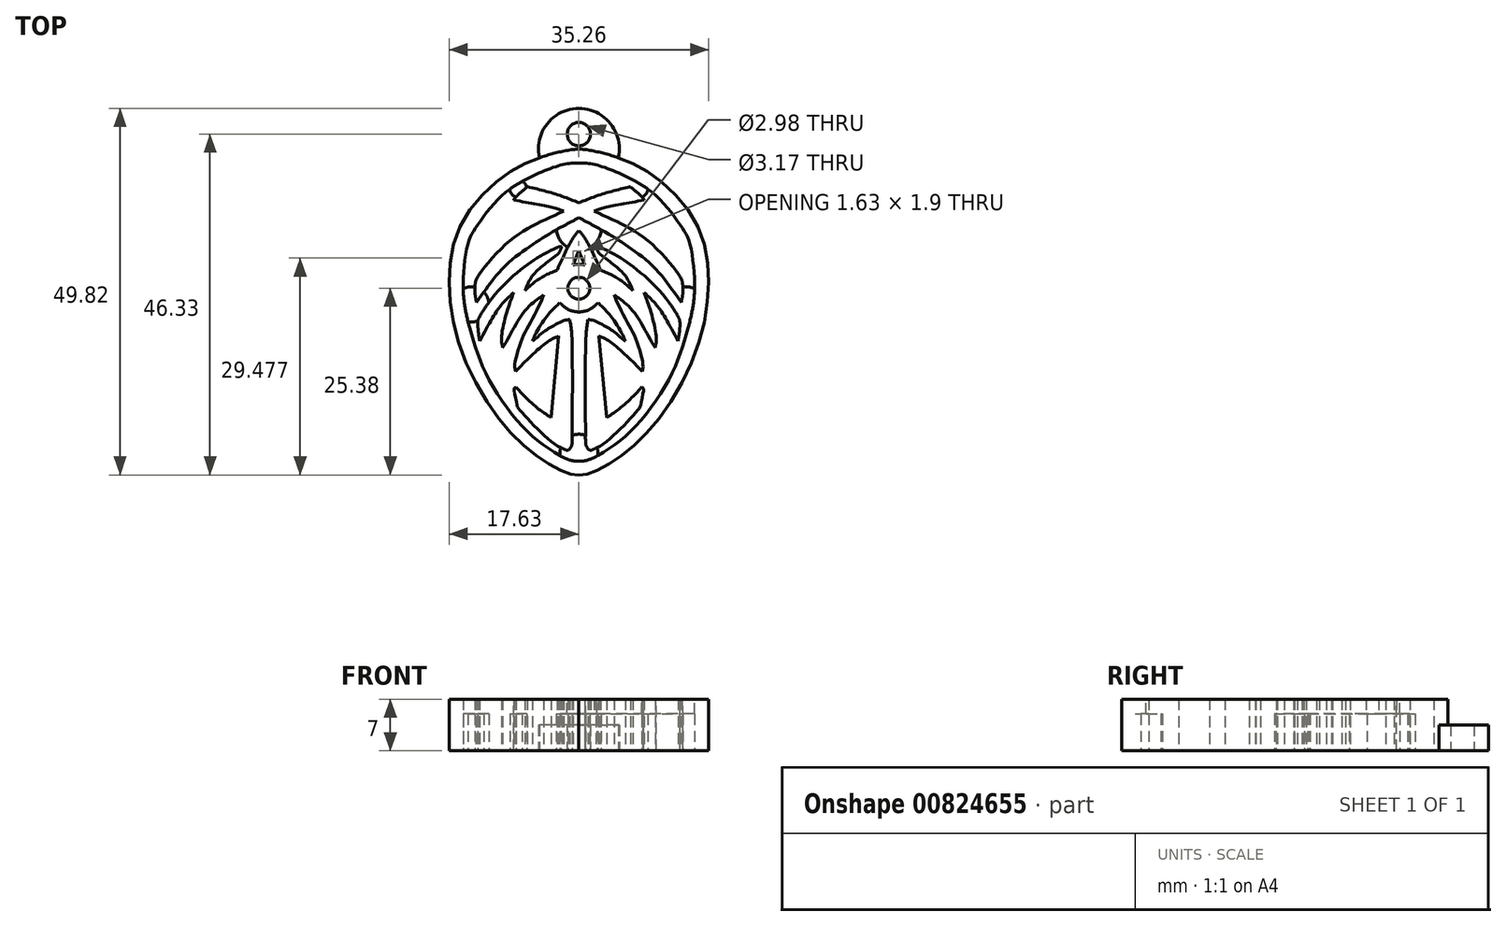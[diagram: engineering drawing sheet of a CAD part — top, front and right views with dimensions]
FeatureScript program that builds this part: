
annotation { "Feature Type Name" : "Feature", "Feature Type Description" : "" }
export const myFeature = defineFeature(function(context is Context, id is Id, definition is map)
    precondition{}
    {
        {
            var Q0;
            Q0=qCreatedBy(makeId("Top.planeOp"),FACE);
            var sketch = newSketch(context, id + "F0", { "sketchPlane" : qUnion([Q0])});
            skFitSpline(sketch, "E0", {"points": [v(2.55, 25.45) * mm, v(-2.7, 24.29) * mm, v(-8.08, 21.4) * mm, v(-13.57, 15.03) * mm, v(-15.07, 6.87) * mm, v(-13.12, -2.73) * mm, v(-7.8, -11.88) * mm, v(-2.92, -16.48) * mm, v(0.86, -18.6) * mm, v(2.55, -18.87) * mm], "startDerivative": vector(-44.7, -3.5) * mm, "endDerivative": vector(27.22, -1.63) * mm});
            skFitSpline(sketch, "E1", {"points": [v(2.55, 18.13) * mm, v(-0.67, 19.32) * mm, v(-4.44, 20.32) * mm], "startDerivative": vector(-6.5, 2.6) * mm, "endDerivative": vector(-7.48, 1.8) * mm});
            skFitSpline(sketch, "E2", {"points": [v(-4.44, 20.32) * mm, v(-6.08, 18.85) * mm, v(-6.33, 18.5) * mm], "startDerivative": vector(-2.9, -2.46) * mm, "endDerivative": vector(-0.57, -1.02) * mm});
            skFitSpline(sketch, "E3", {"points": [v(-6.33, 18.5) * mm, v(-1.03, 17.47) * mm, v(0.5, 17) * mm], "startDerivative": vector(9.43, -1.66) * mm, "endDerivative": vector(3.65, -1.3) * mm});
            skFitSpline(sketch, "E4", {"points": [v(0.5, 17) * mm, v(-3.36, 15.2) * mm, v(-7.38, 12.5) * mm, v(-10.93, 8.48) * mm, v(-11.46, 7.6) * mm], "startDerivative": vector(-14.3, -6.38) * mm, "endDerivative": vector(-2.74, -5.38) * mm});
            skFitSpline(sketch, "E5", {"points": [v(-11.46, 7.6) * mm, v(-11.6, 6.2) * mm, v(-11.36, 4.62) * mm], "startDerivative": vector(-0.47, -2.83) * mm, "endDerivative": vector(0.65, -3.1) * mm});
            skFitSpline(sketch, "E6", {"points": [v(-11.36, 4.62) * mm, v(-10.2, 6.22) * mm, v(-7.6, 9.42) * mm, v(-4.18, 12.14) * mm, v(-1.35, 13.97) * mm, v(2.55, 16.09) * mm], "startDerivative": vector(6.47, 9.1) * mm, "endDerivative": vector(18.2, 9.41) * mm});
            skFitSpline(sketch, "E7", {"points": [v(2.55, 14.35) * mm, v(1.58, 13.08) * mm, v(0.45, 10.83) * mm, v(-0.41, 8.97) * mm], "startDerivative": vector(-3.29, -3.87) * mm, "endDerivative": vector(-2.46, -5.31) * mm});
            skFitSpline(sketch, "E8", {"points": [v(-0.41, 8.97) * mm, v(-2.3, 8.11) * mm, v(-3.85, 7.03) * mm, v(-4.77, 6.2) * mm], "startDerivative": vector(-5.25, -2.13) * mm, "endDerivative": vector(-2.99, -2.86) * mm});
            skFitSpline(sketch, "E9", {"points": [v(-4.77, 6.2) * mm, v(-3.94, 7.95) * mm, v(-2.41, 9.53) * mm, v(-0.41, 11.05) * mm], "startDerivative": vector(2.23, 5.79) * mm, "endDerivative": vector(5.76, 4.22) * mm});
            skFitSpline(sketch, "E10", {"points": [v(-0.41, 11.05) * mm, v(-0.12, 11.36) * mm, v(0.22, 12.2) * mm], "startDerivative": vector(0.74, 0.63) * mm, "endDerivative": vector(0.53, 1.6) * mm});
            skFitSpline(sketch, "E11", {"points": [v(0.22, 12.2) * mm, v(-0.19, 12.11) * mm, v(-2.32, 11.1) * mm, v(-4.77, 9.47) * mm, v(-8.55, 6.02) * mm, v(-10.77, 2.94) * mm, v(-11.16, 2.18) * mm], "startDerivative": vector(-4.53, -0.59) * mm, "endDerivative": vector(-2.94, -6.3) * mm});
            skFitSpline(sketch, "E12", {"points": [v(-11.16, 2.18) * mm, v(-11.16, 1.04) * mm, v(-10.93, -0.65) * mm], "startDerivative": vector(-0.1, -2.4) * mm, "endDerivative": vector(0.55, -3.21) * mm});
            skFitSpline(sketch, "E13", {"points": [v(-10.93, -0.65) * mm, v(-8.93, 2.92) * mm, v(-7.77, 4.5) * mm, v(-6.32, 5.92) * mm], "startDerivative": vector(5.09, 9.46) * mm, "endDerivative": vector(5.07, 4.9) * mm});
            skFitSpline(sketch, "E14", {"points": [v(-6.32, 5.92) * mm, v(-7, 3.98) * mm, v(-7.95, 0.06) * mm, v(-7.8, -1.55) * mm], "startDerivative": vector(-1.92, -5.52) * mm, "endDerivative": vector(1.1, -5.1) * mm});
            skFitSpline(sketch, "E15", {"points": [v(-7.8, -1.55) * mm, v(-6.32, 1.06) * mm, v(-4.65, 3.6) * mm, v(-3.18, 4.92) * mm, v(-2.22, 5.63) * mm], "startDerivative": vector(5.6, 8.8) * mm, "endDerivative": vector(4.7, 3.2) * mm});
            skFitSpline(sketch, "E16", {"points": [v(-2.22, 5.63) * mm, v(-2.8, 4.26) * mm, v(-4.1, 1.79) * mm, v(-4.98, 0.06) * mm, v(-5.83, -2.33) * mm, v(-6.16, -3.96) * mm, v(-6.08, -4.82) * mm], "startDerivative": vector(-3.28, -8.26) * mm, "endDerivative": vector(1.2, -7.04) * mm});
            skFitSpline(sketch, "E17", {"points": [v(-6.08, -4.82) * mm, v(-3.67, -2.43) * mm, v(-1.4, -0.57) * mm, v(-0.18, 0) * mm], "startDerivative": vector(6.04, 6.17) * mm, "endDerivative": vector(4.66, 1.76) * mm});
            skFitSpline(sketch, "E18", {"points": [v(-0.18, 0) * mm, v(-1.24, -11.08) * mm], "startDerivative": vector(-1.06, -11.08) * mm, "endDerivative": vector(-1.06, -11.08) * mm});
            skFitSpline(sketch, "E19", {"points": [v(-1.24, -11.08) * mm, v(-3.32, -9.6) * mm, v(-5.35, -7.64) * mm, v(-6, -6.92) * mm], "startDerivative": vector(-5.46, 3.56) * mm, "endDerivative": vector(-2.32, 2.72) * mm});
            skFitSpline(sketch, "E20", {"points": [v(-6, -6.92) * mm, v(-6.2, -7.08) * mm, v(-6.2, -7.55) * mm, v(-5.83, -9.43) * mm, v(-5.67, -9.8) * mm, v(-4.72, -10.9) * mm, v(-2.58, -13.12) * mm, v(-0.48, -14.85) * mm, v(0.93, -15.54) * mm], "startDerivative": vector(-4.2, -2.56) * mm, "endDerivative": vector(9.93, -4.08) * mm});
            skFitSpline(sketch, "E21", {"points": [v(0.93, -15.54) * mm, v(1.26, -15.39) * mm, v(1.56, -14.87) * mm, v(1.66, -13.25) * mm, v(1.6, 0) * mm, v(1.43, 1.48) * mm, v(1.3, 2.26) * mm], "startDerivative": vector(4.74, 1.36) * mm, "endDerivative": vector(-1.2, 7.65) * mm});
            skFitSpline(sketch, "E22", {"points": [v(1.3, 2.26) * mm, v(0.48, 2.1) * mm, v(-1.04, 1.34) * mm, v(-2.32, 0.51) * mm, v(-3.51, -0.5) * mm, v(-3.75, -0.7) * mm], "startDerivative": vector(-4.36, -0.39) * mm, "endDerivative": vector(-1.78, -1.4) * mm});
            skFitSpline(sketch, "E23", {"points": [v(-3.75, -0.7) * mm, v(-3.55, -0.14) * mm, v(-2.12, 2.26) * mm, v(-0.8, 3.8) * mm, v(-0.07, 4.53) * mm], "startDerivative": vector(0.8, 2.85) * mm, "endDerivative": vector(3.33, 3.29) * mm});
            skFitSpline(sketch, "E24", {"points": [v(-0.07, 4.53) * mm, v(0.22, 4.26) * mm, v(1.3, 3.53) * mm, v(2.55, 3.27) * mm], "startDerivative": vector(1.08, -1.1) * mm, "endDerivative": vector(3.2, -0.3) * mm});
            skFitSpline(sketch, "E25", {"points": [v(2.55, -17.01) * mm, v(1.35, -16.86) * mm, v(-2.05, -14.97) * mm, v(-5.84, -11.48) * mm, v(-9.78, -5.72) * mm, v(-11.64, -1.07) * mm, v(-12.8, 3.23) * mm, v(-13.17, 7.44) * mm, v(-12.47, 12.78) * mm, v(-11.46, 14.74) * mm, v(-8.46, 18.59) * mm, v(-4.42, 21.43) * mm, v(0.2, 23.27) * mm, v(2.55, 23.55) * mm], "startDerivative": vector(-25.48, 0.12) * mm, "endDerivative": vector(36.78, 1.36) * mm});
            skFitSpline(sketch, "E26", {"points": [v(2.55, 11.56) * mm, v(1.73, 9.66) * mm], "startDerivative": vector(-0.82, -1.9) * mm, "endDerivative": vector(-0.82, -1.9) * mm});
            skFitSpline(sketch, "E27", {"points": [v(1.73, 9.66) * mm, v(2.21, 9.74) * mm, v(2.55, 9.75) * mm], "startDerivative": vector(0.92, 0.2) * mm, "endDerivative": vector(0.7, 0) * mm});
            skCircle(sketch, "E28", {"center": v(2.55, 6.5) * mm, "radius": 1.49 * mm});
            skFitSpline(sketch, "E29.MirrorCS", {"points": [v(2.55, -17.01) * mm, v(3.75, -16.86) * mm, v(7.15, -14.97) * mm, v(10.94, -11.48) * mm, v(14.88, -5.72) * mm, v(16.74, -1.07) * mm, v(17.9, 3.23) * mm, v(18.27, 7.44) * mm, v(17.56, 12.78) * mm, v(16.56, 14.74) * mm, v(13.56, 18.59) * mm, v(9.52, 21.43) * mm, v(4.9, 23.27) * mm, v(2.55, 23.55) * mm], "startDerivative": vector(25.48, 0.12) * mm, "endDerivative": vector(-36.78, 1.36) * mm});
            skFitSpline(sketch, "E30.MirrorCS", {"points": [v(2.55, 25.45) * mm, v(7.8, 24.29) * mm, v(13.18, 21.4) * mm, v(18.67, 15.03) * mm, v(20.17, 6.87) * mm, v(18.22, -2.73) * mm, v(12.9, -11.88) * mm, v(8.02, -16.48) * mm, v(4.24, -18.6) * mm, v(2.55, -18.87) * mm], "startDerivative": vector(44.7, -3.5) * mm, "endDerivative": vector(-27.22, -1.63) * mm});
            skFitSpline(sketch, "E31.MirrorCS", {"points": [v(2.55, 18.13) * mm, v(5.77, 19.32) * mm, v(9.54, 20.32) * mm], "startDerivative": vector(6.5, 2.6) * mm, "endDerivative": vector(7.48, 1.8) * mm});
            skFitSpline(sketch, "E32.MirrorCS", {"points": [v(11.43, 18.5) * mm, v(6.13, 17.47) * mm, v(4.6, 17) * mm], "startDerivative": vector(-9.43, -1.66) * mm, "endDerivative": vector(-3.65, -1.3) * mm});
            skFitSpline(sketch, "E33.MirrorCS", {"points": [v(4.6, 17) * mm, v(8.46, 15.2) * mm, v(12.48, 12.5) * mm, v(16.03, 8.48) * mm, v(16.56, 7.6) * mm], "startDerivative": vector(14.3, -6.38) * mm, "endDerivative": vector(2.74, -5.38) * mm});
            skFitSpline(sketch, "E34.MirrorCS", {"points": [v(16.46, 4.62) * mm, v(15.3, 6.22) * mm, v(12.7, 9.42) * mm, v(9.28, 12.14) * mm, v(6.45, 13.97) * mm, v(2.55, 16.09) * mm], "startDerivative": vector(-6.47, 9.1) * mm, "endDerivative": vector(-18.2, 9.41) * mm});
            skFitSpline(sketch, "E35.MirrorCS", {"points": [v(4.88, 12.2) * mm, v(5.28, 12.11) * mm, v(7.42, 11.1) * mm, v(9.87, 9.47) * mm, v(13.65, 6.02) * mm, v(15.87, 2.94) * mm, v(16.26, 2.18) * mm], "startDerivative": vector(4.53, -0.59) * mm, "endDerivative": vector(2.94, -6.3) * mm});
            skFitSpline(sketch, "E36.MirrorCS", {"points": [v(2.55, 14.35) * mm, v(3.52, 13.08) * mm, v(4.65, 10.83) * mm, v(5.51, 8.97) * mm], "startDerivative": vector(3.29, -3.87) * mm, "endDerivative": vector(2.46, -5.31) * mm});
            skFitSpline(sketch, "E37.MirrorCS", {"points": [v(9.87, 6.2) * mm, v(9.04, 7.95) * mm, v(7.51, 9.53) * mm, v(5.51, 11.05) * mm], "startDerivative": vector(-2.23, 5.79) * mm, "endDerivative": vector(-5.76, 4.22) * mm});
            skFitSpline(sketch, "E38.MirrorCS", {"points": [v(16.03, -0.65) * mm, v(14.03, 2.92) * mm, v(12.87, 4.5) * mm, v(11.42, 5.92) * mm], "startDerivative": vector(-5.09, 9.46) * mm, "endDerivative": vector(-5.07, 4.9) * mm});
            skFitSpline(sketch, "E39.MirrorCS", {"points": [v(16.26, 2.18) * mm, v(16.26, 1.04) * mm, v(16.03, -0.65) * mm], "startDerivative": vector(0.1, -2.4) * mm, "endDerivative": vector(-0.55, -3.21) * mm});
            skFitSpline(sketch, "E40.MirrorCS", {"points": [v(16.56, 7.6) * mm, v(16.7, 6.2) * mm, v(16.46, 4.62) * mm], "startDerivative": vector(0.47, -2.83) * mm, "endDerivative": vector(-0.65, -3.1) * mm});
            skFitSpline(sketch, "E41.MirrorCS", {"points": [v(7.32, 5.63) * mm, v(7.9, 4.26) * mm, v(9.2, 1.79) * mm, v(10.08, 0.06) * mm, v(10.93, -2.33) * mm, v(11.26, -3.96) * mm, v(11.18, -4.82) * mm], "startDerivative": vector(3.28, -8.26) * mm, "endDerivative": vector(-1.2, -7.04) * mm});
            skFitSpline(sketch, "E42.MirrorCS", {"points": [v(12.9, -1.55) * mm, v(11.42, 1.06) * mm, v(9.75, 3.6) * mm, v(8.28, 4.92) * mm, v(7.32, 5.63) * mm], "startDerivative": vector(-5.6, 8.8) * mm, "endDerivative": vector(-4.7, 3.2) * mm});
            skFitSpline(sketch, "E43.MirrorCS", {"points": [v(11.42, 5.92) * mm, v(12.1, 3.98) * mm, v(13.04, 0.06) * mm, v(12.9, -1.55) * mm], "startDerivative": vector(1.92, -5.52) * mm, "endDerivative": vector(-1.1, -5.1) * mm});
            skFitSpline(sketch, "E44.MirrorCS", {"points": [v(11.18, -4.82) * mm, v(8.77, -2.43) * mm, v(6.5, -0.57) * mm, v(5.28, 0) * mm], "startDerivative": vector(-6.04, 6.17) * mm, "endDerivative": vector(-4.66, 1.76) * mm});
            skFitSpline(sketch, "E45.MirrorCS", {"points": [v(3.8, 2.26) * mm, v(4.62, 2.1) * mm, v(6.14, 1.34) * mm, v(7.42, 0.51) * mm, v(8.61, -0.5) * mm, v(8.85, -0.7) * mm], "startDerivative": vector(4.36, -0.39) * mm, "endDerivative": vector(1.78, -1.4) * mm});
            skFitSpline(sketch, "E46.MirrorCS", {"points": [v(8.85, -0.7) * mm, v(8.65, -0.14) * mm, v(7.22, 2.26) * mm, v(5.9, 3.8) * mm, v(5.17, 4.53) * mm], "startDerivative": vector(-0.8, 2.85) * mm, "endDerivative": vector(-3.33, 3.29) * mm});
            skFitSpline(sketch, "E47.MirrorCS", {"points": [v(5.17, 4.53) * mm, v(4.88, 4.26) * mm, v(3.8, 3.53) * mm, v(2.55, 3.27) * mm], "startDerivative": vector(-1.08, -1.1) * mm, "endDerivative": vector(-3.2, -0.3) * mm});
            skFitSpline(sketch, "E48.MirrorCS", {"points": [v(4.17, -15.54) * mm, v(3.84, -15.39) * mm, v(3.54, -14.87) * mm, v(3.44, -13.25) * mm, v(3.5, 0) * mm, v(3.67, 1.48) * mm, v(3.8, 2.26) * mm], "startDerivative": vector(-4.74, 1.36) * mm, "endDerivative": vector(1.2, 7.65) * mm});
            skFitSpline(sketch, "E49.MirrorCS", {"points": [v(5.28, 0) * mm, v(6.34, -11.08) * mm], "startDerivative": vector(1.06, -11.08) * mm, "endDerivative": vector(1.06, -11.08) * mm});
            skFitSpline(sketch, "E50.MirrorCS", {"points": [v(11.1, -6.92) * mm, v(11.3, -7.08) * mm, v(11.3, -7.55) * mm, v(10.93, -9.43) * mm, v(10.77, -9.8) * mm, v(9.82, -10.9) * mm, v(7.68, -13.12) * mm, v(5.58, -14.85) * mm, v(4.17, -15.54) * mm], "startDerivative": vector(4.2, -2.56) * mm, "endDerivative": vector(-9.93, -4.08) * mm});
            skFitSpline(sketch, "E51.MirrorCS", {"points": [v(6.34, -11.08) * mm, v(8.42, -9.6) * mm, v(10.45, -7.64) * mm, v(11.1, -6.92) * mm], "startDerivative": vector(5.46, 3.56) * mm, "endDerivative": vector(2.32, 2.72) * mm});
            skFitSpline(sketch, "E52.MirrorCS", {"points": [v(2.55, 11.56) * mm, v(3.37, 9.66) * mm], "startDerivative": vector(0.82, -1.9) * mm, "endDerivative": vector(0.82, -1.9) * mm});
            skFitSpline(sketch, "E53.MirrorCS", {"points": [v(3.37, 9.66) * mm, v(2.88, 9.74) * mm, v(2.55, 9.75) * mm], "startDerivative": vector(-0.92, 0.2) * mm, "endDerivative": vector(-0.7, 0) * mm});
            skFitSpline(sketch, "E54.MirrorCS", {"points": [v(9.54, 20.32) * mm, v(11.18, 18.85) * mm, v(11.43, 18.5) * mm], "startDerivative": vector(2.9, -2.46) * mm, "endDerivative": vector(0.57, -1.02) * mm});
            skFitSpline(sketch, "E55.MirrorCS", {"points": [v(5.51, 11.05) * mm, v(5.22, 11.36) * mm, v(4.88, 12.2) * mm], "startDerivative": vector(-0.74, 0.63) * mm, "endDerivative": vector(-0.53, 1.6) * mm});
            skFitSpline(sketch, "E56.MirrorCS", {"points": [v(5.51, 8.97) * mm, v(7.4, 8.11) * mm, v(8.95, 7.03) * mm, v(9.87, 6.2) * mm], "startDerivative": vector(5.25, -2.13) * mm, "endDerivative": vector(2.99, -2.86) * mm});
            skArc(sketch, "E57", {"start": v(-0.5, 14.46) * mm, "mid": v(-0.02, 13.08) * mm, "end": v(1.03, 12.07) * mm});
            skArc(sketch, "E58.trimOffspring", {"start": v(4.07, 12.07) * mm, "mid": v(5.12, 13.08) * mm, "end": v(5.6, 14.46) * mm});
            skArc(sketch, "E59", {"start": v(0.08, -15.16) * mm, "mid": v(-0.02, -15.7) * mm, "end": v(0, -16.25) * mm});
            skArc(sketch, "E60.trimOffspring", {"start": v(3.44, -13.5) * mm, "mid": v(2.55, -13.34) * mm, "end": v(1.66, -13.5) * mm});
            skArc(sketch, "E61.trimOffspring", {"start": v(5.1, -16.25) * mm, "mid": v(5.12, -15.7) * mm, "end": v(5.02, -15.16) * mm});
            skArc(sketch, "E62", {"start": v(-12.51, 1.96) * mm, "mid": v(-11.83, 1.93) * mm, "end": v(-11.16, 2.1) * mm});
            skArc(sketch, "E63.trimOffspring", {"start": v(-9.7, 4.59) * mm, "mid": v(-9.91, 5.34) * mm, "end": v(-10.37, 5.99) * mm});
            skArc(sketch, "E64.trimOffspring", {"start": v(-11.59, 6.66) * mm, "mid": v(-12.4, 6.68) * mm, "end": v(-13.17, 6.44) * mm});
            skArc(sketch, "E65.MirrorCS", {"start": v(16.69, 6.66) * mm, "mid": v(17.5, 6.68) * mm, "end": v(18.27, 6.44) * mm});
            skArc(sketch, "E66.MirrorCS", {"start": v(14.8, 4.59) * mm, "mid": v(15.01, 5.34) * mm, "end": v(15.46, 5.99) * mm});
            skArc(sketch, "E67.MirrorCS", {"start": v(17.6, 1.96) * mm, "mid": v(16.93, 1.93) * mm, "end": v(16.26, 2.1) * mm});
            skArc(sketch, "E68", {"start": v(-6.83, 19.99) * mm, "mid": v(-6.59, 19.33) * mm, "end": v(-6, 18.93) * mm});
            skArc(sketch, "E69.MirrorC", {"start": v(11.92, 19.99) * mm, "mid": v(11.69, 19.33) * mm, "end": v(11.1, 18.93) * mm});
            skArc(sketch, "E70.trimOffspring", {"start": v(-4.54, 20.24) * mm, "mid": v(-4.75, 20.71) * mm, "end": v(-5.14, 21.05) * mm});
            skArc(sketch, "E71.trimOffspring", {"start": v(9.64, 20.24) * mm, "mid": v(9.85, 20.71) * mm, "end": v(10.24, 21.05) * mm});
            skLineSegment(sketch, "E72", {"start": v(2.55, 25.45) * mm, "end": v(2.55, -18.87) * mm});
            skLineSegment(sketch, "E73.bottom", {"start": v(23.35, -20.1) * mm, "end": v(-17.3, -20.1) * mm});
            skLineSegment(sketch, "E73.left", {"start": v(23.35, -20.1) * mm, "end": v(23.35, 29.9) * mm});
            skLineSegment(sketch, "E73.right", {"start": v(-17.3, -20.1) * mm, "end": v(-17.3, 29.9) * mm});
            skArc(sketch, "E74", {"start": v(7.92, 24.25) * mm, "mid": v(2.55, 30.95) * mm, "end": v(-2.82, 24.25) * mm});
            skCircle(sketch, "E75", {"center": v(2.55, 27.46) * mm, "radius": 1.59 * mm});
            skSolve(sketch);
        }
        {
            var Q0;
            {var subQ16=sQuery(id+"F0.wireOp",EDGE,"E1");Q0=makeQuery(id+"F0.imprint","IMPRINT",FACE,{"disambiguationData":[TD([[makeQuery(id+"F0.imprint","IMPRINT",EDGE,{"derivedFrom":subQ16}),1.0]])]});}
            var Q1;
            {var subQ19=sQuery(id+"F0.wireOp",EDGE,"E8");Q1=makeQuery(id+"F0.imprint","IMPRINT",FACE,{"disambiguationData":[TD([[makeQuery(id+"F0.imprint","IMPRINT",EDGE,{"derivedFrom":subQ19}),1.0]])]});}
            var Q2;
            {var subQ3=sQuery(id+"F0.wireOp",EDGE,"E30.MirrorCS");var subQ4=sQuery(id+"F0.wireOp",EDGE,"E0");var subQ5=makeQuery(id+"F0.imprint","INTERSECT",VERTEX,{"disambiguationData":[OD(0.0)],"derivedFrom":[subQ4,subQ3]});Q2=makeQuery(id+"F0.imprint","IMPRINT",FACE,{"disambiguationData":[TD([[makeQuery(id+"F0.imprint","IMPRINT",EDGE,{"disambiguationData":[TD([[subQ5,-1.0]])],"derivedFrom":subQ4}),1.0]])]});}
            var Q3;
            {var subQ0=sQuery(id+"F0.wireOp",EDGE,"E29.MirrorCS");var subQ4=makeQuery(id+"F0.imprint","INTERSECT",VERTEX,{"derivedFrom":[subQ0,sQuery(id+"F0.wireOp",EDGE,"E61.trimOffspring")]});Q3=makeQuery(id+"F0.imprint","IMPRINT",FACE,{"disambiguationData":[TD([[makeQuery(id+"F0.imprint","IMPRINT",EDGE,{"disambiguationData":[TD([[subQ4,-1.0]])],"derivedFrom":subQ0}),-1.0]])]});}
            var Q4;
            {var subQ3=sQuery(id+"F0.wireOp",EDGE,"E31.MirrorCS");Q4=makeQuery(id+"F0.imprint","IMPRINT",FACE,{"disambiguationData":[TD([[makeQuery(id+"F0.imprint","IMPRINT",EDGE,{"derivedFrom":subQ3}),-1.0]])]});}
            var Q5;
            Q5=makeQuery(id+"F0.imprint","IMPRINT",FACE,{"disambiguationData":[TD([[makeQuery(id+"F0.imprint","IMPRINT",EDGE,{"derivedFrom":sQuery(id+"F0.wireOp",EDGE,"E37.MirrorCS")}),-1.0]])]});
            extrude(context, id + "F1", {"entities" : qUnion([Q0, Q1, Q2, Q3, Q4, Q5]), "depth" : 7 * mm, "offsetDistance" : 25 * mm});
        }
        {
            var Q0;
            {var subQ0=sQuery(id+"F0.wireOp",EDGE,"E68");Q0=makeQuery(id+"F0.imprint","IMPRINT",FACE,{"disambiguationData":[TD([[makeQuery(id+"F0.imprint","IMPRINT",EDGE,{"derivedFrom":subQ0}),1.0]])]});}
            var Q1;
            {var subQ7=sQuery(id+"F0.wireOp",EDGE,"E57");Q1=makeQuery(id+"F0.imprint","IMPRINT",FACE,{"disambiguationData":[TD([[makeQuery(id+"F0.imprint","IMPRINT",EDGE,{"derivedFrom":subQ7}),1.0]])]});}
            var Q2;
            {var subQ0=sQuery(id+"F0.wireOp",EDGE,"E69.MirrorC");Q2=makeQuery(id+"F0.imprint","IMPRINT",FACE,{"disambiguationData":[TD([[makeQuery(id+"F0.imprint","IMPRINT",EDGE,{"derivedFrom":subQ0}),-1.0]])]});}
            var Q3;
            {var subQ8=sQuery(id+"F0.wireOp",EDGE,"E65.MirrorCS");Q3=makeQuery(id+"F0.imprint","IMPRINT",FACE,{"disambiguationData":[TD([[makeQuery(id+"F0.imprint","IMPRINT",EDGE,{"derivedFrom":subQ8}),-1.0]])]});}
            var Q4;
            {var subQ3=sQuery(id+"F0.wireOp",EDGE,"E62");Q4=makeQuery(id+"F0.imprint","IMPRINT",FACE,{"disambiguationData":[TD([[makeQuery(id+"F0.imprint","IMPRINT",EDGE,{"derivedFrom":subQ3}),1.0]])]});}
            var Q5;
            {var subQ3=sQuery(id+"F0.wireOp",EDGE,"E59");Q5=makeQuery(id+"F0.imprint","IMPRINT",FACE,{"disambiguationData":[TD([[makeQuery(id+"F0.imprint","IMPRINT",EDGE,{"derivedFrom":subQ3}),1.0]])]});}
            var Q6;
            {var subQ3=sQuery(id+"F0.wireOp",EDGE,"E58.trimOffspring");Q6=makeQuery(id+"F0.imprint","IMPRINT",FACE,{"disambiguationData":[TD([[makeQuery(id+"F0.imprint","IMPRINT",EDGE,{"derivedFrom":subQ3}),1.0]])]});}
            var Q7;
            {var subQ7=sQuery(id+"F0.wireOp",EDGE,"E61.trimOffspring");Q7=makeQuery(id+"F0.imprint","IMPRINT",FACE,{"disambiguationData":[TD([[makeQuery(id+"F0.imprint","IMPRINT",EDGE,{"derivedFrom":subQ7}),1.0]])]});}
            extrude(context, id + "F2", {"entities" : qUnion([Q0, Q1, Q2, Q3, Q4, Q5, Q6, Q7]), "operationType" : NewBodyOperationType.ADD, "depth" : 5 * mm, "offsetDistance" : 25 * mm});
        }
        {
            var Q0;
            {var subQ3=sQuery(id+"F0.wireOp",EDGE,"E74");Q0=makeQuery(id+"F0.imprint","IMPRINT",FACE,{"disambiguationData":[TD([[makeQuery(id+"F0.imprint","IMPRINT",EDGE,{"derivedFrom":subQ3}),1.0]])]});}
            extrude(context, id + "F3", {"entities" : qUnion([Q0]), "operationType" : NewBodyOperationType.ADD, "depth" : 3.5 * mm, "offsetDistance" : 25 * mm});
        }
    });
